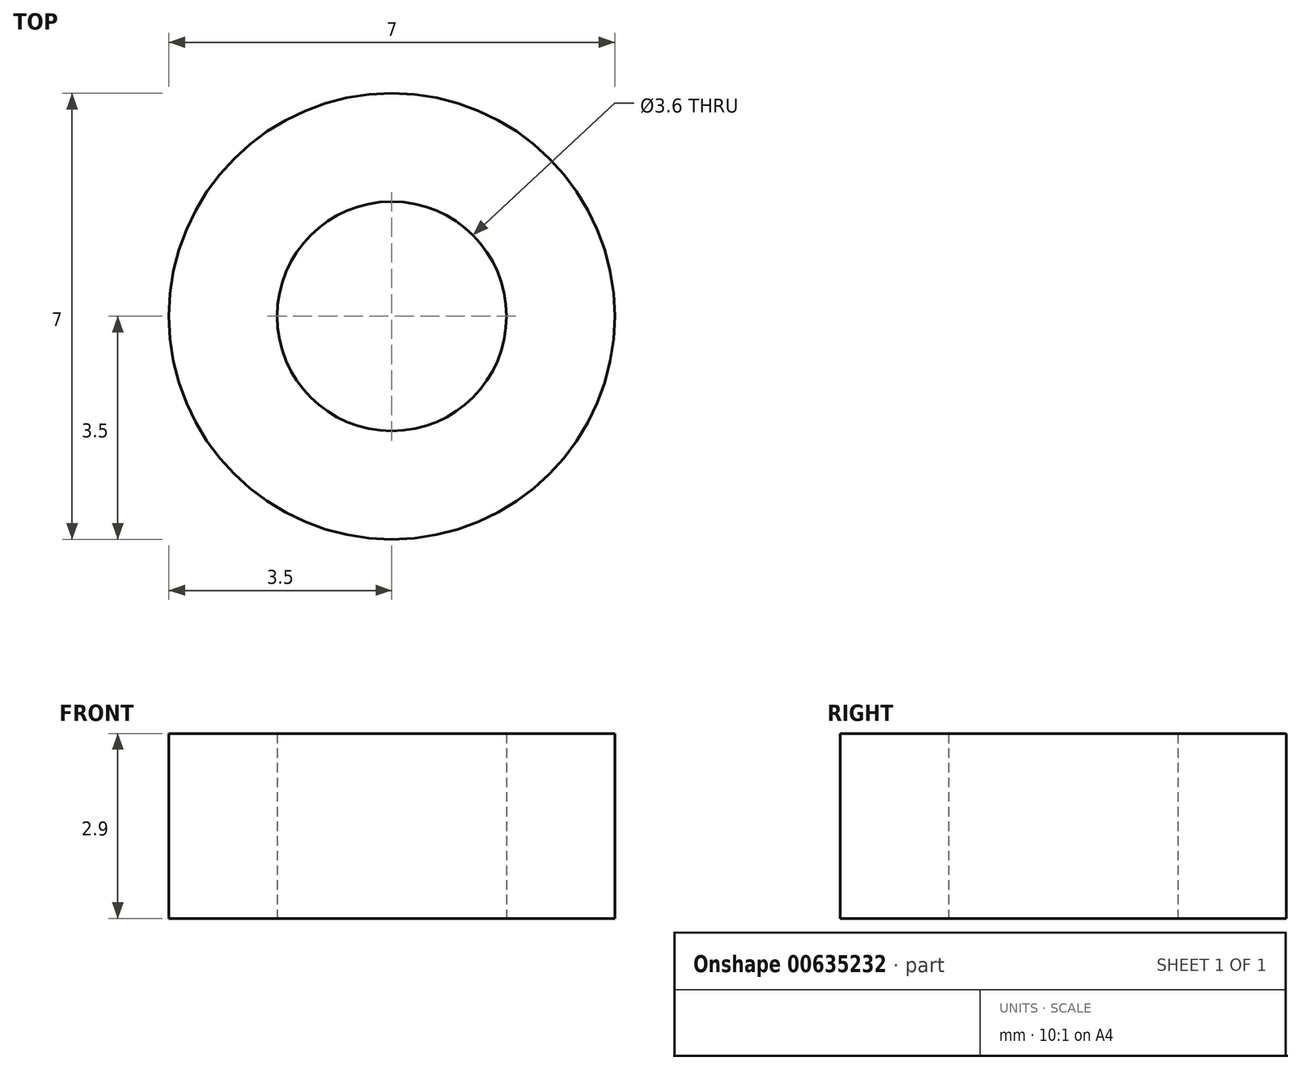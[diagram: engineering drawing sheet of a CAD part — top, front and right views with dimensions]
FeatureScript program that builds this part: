
annotation { "Feature Type Name" : "Feature", "Feature Type Description" : "" }
export const myFeature = defineFeature(function(context is Context, id is Id, definition is map)
    precondition{}
    {
        {
            var Q0;
            Q0=qCreatedBy(makeId("Top.planeOp"),FACE);
            var sketch = newSketch(context, id + "F0", { "sketchPlane" : qUnion([Q0])});
            skCircle(sketch, "E0", {"center": v(0, 0) * mm, "radius": 3.5 * mm});
            skCircle(sketch, "E1", {"center": v(0, 0) * mm, "radius": 1.8 * mm});
            skSolve(sketch);
        }
        {
            var Q0;
            Q0=makeQuery(id+"F0.imprint","IMPRINT",FACE,{"disambiguationData":[TD([[makeQuery(id+"F0.imprint","IMPRINT",EDGE,{"derivedFrom":sQuery(id+"F0.wireOp",EDGE,"E0")}),1.0]])]});
            extrude(context, id + "F1", {"entities" : qUnion([Q0]), "depth" : 2.9 * mm, "offsetDistance" : 25 * mm});
        }
    });
